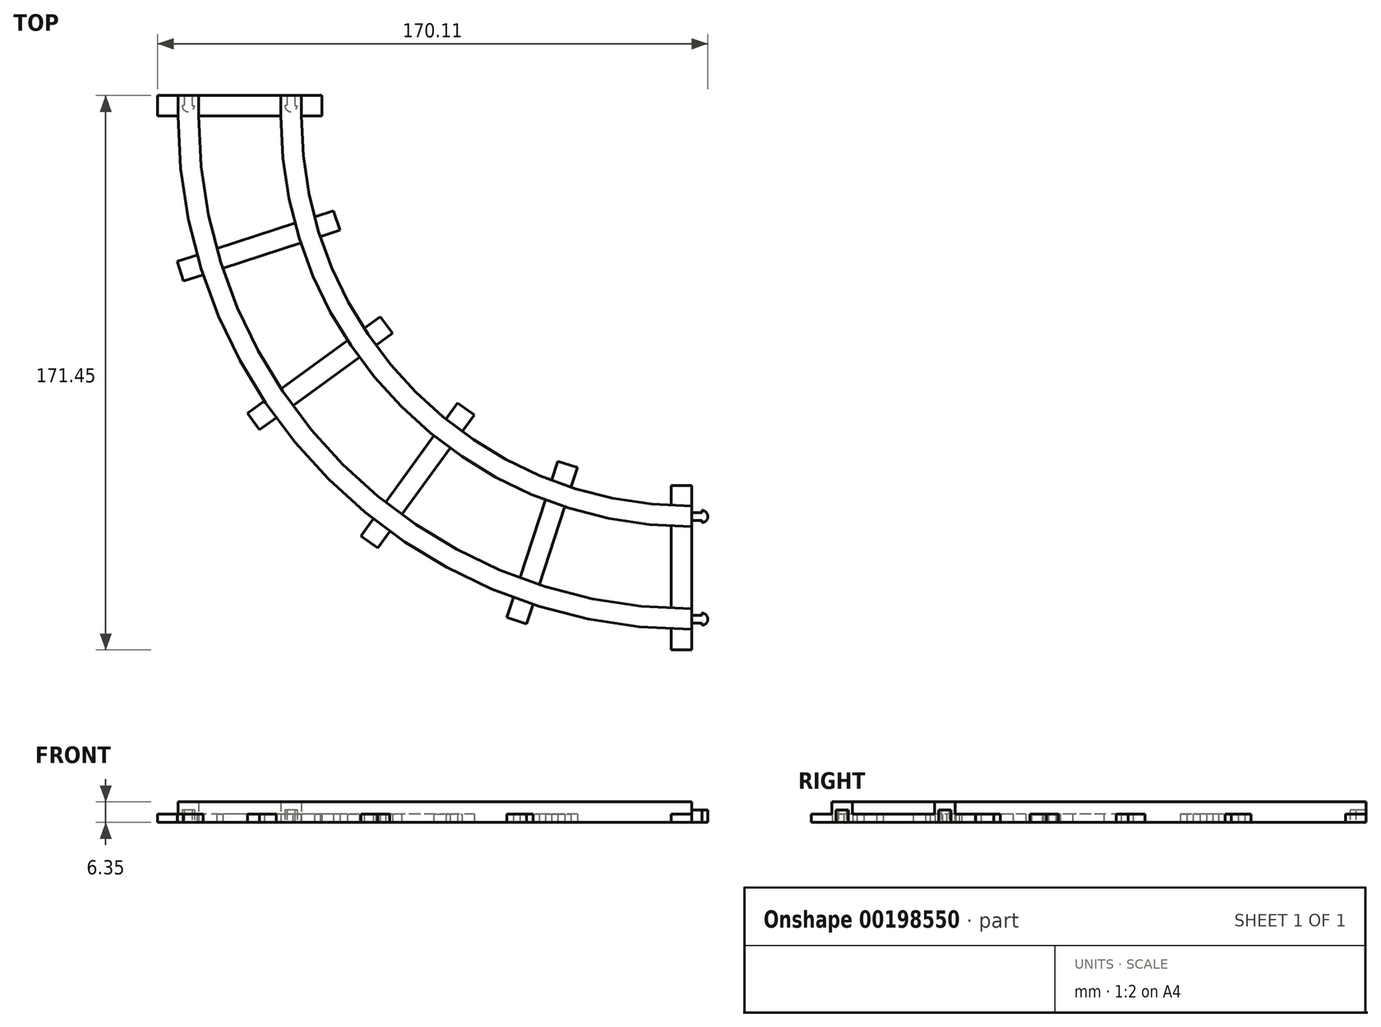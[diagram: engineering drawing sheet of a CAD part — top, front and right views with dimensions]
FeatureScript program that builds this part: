
annotation { "Feature Type Name" : "Feature", "Feature Type Description" : "" }
export const myFeature = defineFeature(function(context is Context, id is Id, definition is map)
    precondition{}
    {
        {
            var Q0;
            Q0=qCreatedBy(makeId("Top.planeOp"),FACE);
            var sketch = newSketch(context, id + "F0", { "sketchPlane" : qUnion([Q0])});
            skLineSegment(sketch, "E0.bottom", {"start": v(76.2, 76.2) * mm, "end": v(-76.2, 76.2) * mm, "construction": true});
            skPoint(sketch, "E0.middle", {"position": v(0, 0) * mm});
            skLineSegment(sketch, "E1", {"start": v(-76.2, 76.2) * mm, "end": v(-76.2, 101.6) * mm, "construction": true});
            skLineSegment(sketch, "E2", {"start": v(76.2, -76.2) * mm, "end": v(101.6, -76.2) * mm, "construction": true});
            skArc(sketch, "E3", {"start": v(76.2, -76.2) * mm, "mid": v(-31.56, -31.56) * mm, "end": v(-76.2, 76.2) * mm});
            skLineSegment(sketch, "E4", {"start": v(-76.2, 76.2) * mm, "end": v(-50.8, 76.2) * mm, "construction": true});
            skLineSegment(sketch, "E5", {"start": v(-50.8, 76.2) * mm, "end": v(-50.8, 101.6) * mm, "construction": true});
            skLineSegment(sketch, "E6", {"start": v(76.2, -76.2) * mm, "end": v(76.2, -50.8) * mm, "construction": true});
            skLineSegment(sketch, "E7", {"start": v(76.2, -50.8) * mm, "end": v(101.6, -50.8) * mm, "construction": true});
            skArc(sketch, "E8", {"start": v(76.2, -50.8) * mm, "mid": v(-13.6, -13.6) * mm, "end": v(-50.8, 76.2) * mm});
            skLineSegment(sketch, "E9", {"start": v(-76.2, 76.2) * mm, "end": v(-82.55, 76.2) * mm, "construction": true});
            skLineSegment(sketch, "E10", {"start": v(76.2, -76.2) * mm, "end": v(76.2, -82.55) * mm, "construction": true});
            skLineSegment(sketch, "E11", {"start": v(76.2, -82.55) * mm, "end": v(101.6, -82.55) * mm, "construction": true});
            skArc(sketch, "E12", {"start": v(76.2, -82.55) * mm, "mid": v(-36.05, -36.05) * mm, "end": v(-82.55, 76.2) * mm});
            skLineSegment(sketch, "E13", {"start": v(-82.55, 76.2) * mm, "end": v(-76.2, 76.2) * mm});
            skLineSegment(sketch, "E14", {"start": v(76.2, -82.55) * mm, "end": v(76.2, -76.2) * mm});
            skLineSegment(sketch, "E15", {"start": v(-50.8, 76.2) * mm, "end": v(-44.45, 76.2) * mm});
            skLineSegment(sketch, "E16", {"start": v(-44.45, 76.2) * mm, "end": v(-44.45, 101.6) * mm, "construction": true});
            skLineSegment(sketch, "E17", {"start": v(76.2, -44.45) * mm, "end": v(101.6, -44.45) * mm, "construction": true});
            skArc(sketch, "E18", {"start": v(76.2, -44.45) * mm, "mid": v(-9.11, -9.11) * mm, "end": v(-44.45, 76.2) * mm});
            skLineSegment(sketch, "E19", {"start": v(76.2, -44.45) * mm, "end": v(76.2, -50.8) * mm});
            skSolve(sketch);
        }
        {
            var Q0;
            Q0 = qSketchRegion(id + "F0", true);
            extrude(context, id + "F1", {"entities" : qUnion([Q0]), "depth" : 6.35 * mm});
        }
        {
            var Q0;
            Q0=qCreatedBy(makeId("Top.planeOp"),FACE);
            var sketch = newSketch(context, id + "F2", { "sketchPlane" : qUnion([Q0])});
            skLineSegment(sketch, "E20.bottom", {"start": v(76.2, 76.2) * mm, "end": v(-76.2, 76.2) * mm, "construction": true});
            skLineSegment(sketch, "E20.top", {"start": v(76.2, -76.2) * mm, "end": v(-76.2, -76.2) * mm, "construction": true});
            skLineSegment(sketch, "E20.right", {"start": v(-76.2, 76.2) * mm, "end": v(-76.2, -76.2) * mm, "construction": true});
            skPoint(sketch, "E20.middle", {"position": v(0, 0) * mm});
            skLineSegment(sketch, "E21", {"start": v(76.2, -76.2) * mm, "end": v(76.2, -88.9) * mm, "construction": true});
            skLineSegment(sketch, "E22", {"start": v(76.2, -76.2) * mm, "end": v(76.2, -38.1) * mm, "construction": true});
            skLineSegment(sketch, "E23", {"start": v(76.2, -38.1) * mm, "end": v(69.85, -38.1) * mm});
            skLineSegment(sketch, "E24", {"start": v(76.2, -88.9) * mm, "end": v(69.85, -88.9) * mm});
            skLineSegment(sketch, "E25", {"start": v(69.85, -38.1) * mm, "end": v(69.85, -88.9) * mm});
            skLineSegment(sketch, "E26", {"start": v(76.2, -38.1) * mm, "end": v(76.2, -88.9) * mm});
            skArc(sketch, "E27.0", {"start": v(76.2, -44.45) * mm, "mid": v(-9.11, -9.11) * mm, "end": v(-44.45, 76.2) * mm, "construction": true});
            skLineSegment(sketch, "E28.1.0", {"start": v(40.88, -32.5) * mm, "end": v(25.18, -80.82) * mm});
            skLineSegment(sketch, "E28.1.1", {"start": v(34.84, -30.54) * mm, "end": v(19.14, -78.86) * mm});
            skLineSegment(sketch, "E28.1.2", {"start": v(40.88, -32.5) * mm, "end": v(34.84, -30.54) * mm});
            skLineSegment(sketch, "E28.1.3", {"start": v(25.18, -80.82) * mm, "end": v(19.14, -78.86) * mm});
            skLineSegment(sketch, "E28.2.0", {"start": v(9.02, -16.27) * mm, "end": v(-20.84, -57.37) * mm});
            skLineSegment(sketch, "E28.2.1", {"start": v(3.88, -12.54) * mm, "end": v(-25.98, -53.64) * mm});
            skLineSegment(sketch, "E28.2.2", {"start": v(9.02, -16.27) * mm, "end": v(3.88, -12.54) * mm});
            skLineSegment(sketch, "E28.2.3", {"start": v(-20.84, -57.37) * mm, "end": v(-25.98, -53.64) * mm});
            skLineSegment(sketch, "E28.3.0", {"start": v(-16.27, 9.02) * mm, "end": v(-57.37, -20.84) * mm});
            skLineSegment(sketch, "E28.3.1", {"start": v(-20, 14.15) * mm, "end": v(-61.1, -15.7) * mm});
            skLineSegment(sketch, "E28.3.2", {"start": v(-16.27, 9.02) * mm, "end": v(-20, 14.15) * mm});
            skLineSegment(sketch, "E28.3.3", {"start": v(-57.37, -20.84) * mm, "end": v(-61.1, -15.7) * mm});
            skLineSegment(sketch, "E28.4.0", {"start": v(-32.5, 40.88) * mm, "end": v(-80.82, 25.18) * mm});
            skLineSegment(sketch, "E28.4.1", {"start": v(-34.47, 46.92) * mm, "end": v(-82.78, 31.22) * mm});
            skLineSegment(sketch, "E28.4.2", {"start": v(-32.5, 40.88) * mm, "end": v(-34.47, 46.92) * mm});
            skLineSegment(sketch, "E28.4.3", {"start": v(-80.82, 25.18) * mm, "end": v(-82.78, 31.22) * mm});
            skLineSegment(sketch, "E28.5.0", {"start": v(-38.1, 76.2) * mm, "end": v(-88.9, 76.2) * mm});
            skLineSegment(sketch, "E28.5.1", {"start": v(-38.1, 82.55) * mm, "end": v(-88.9, 82.55) * mm});
            skLineSegment(sketch, "E28.5.2", {"start": v(-38.1, 76.2) * mm, "end": v(-38.1, 82.55) * mm});
            skLineSegment(sketch, "E28.5.3", {"start": v(-88.9, 76.2) * mm, "end": v(-88.9, 82.55) * mm});
            skLineSegment(sketch, "E28.anchor1", {"start": v(76.2, 76.2) * mm, "end": v(76.2, -88.9) * mm, "construction": true});
            skLineSegment(sketch, "E28.anchor2", {"start": v(76.2, 76.2) * mm, "end": v(-88.9, 76.2) * mm, "construction": true});
            skSolve(sketch);
        }
        {
            var Q0;
            Q0 = qSketchRegion(id + "F2", true);
            extrude(context, id + "F3", {"entities" : qUnion([Q0]), "operationType" : NewBodyOperationType.ADD, "depth" : 2.54 * mm});
        }
        {
            var Q0;
            Q0=qCreatedBy(makeId("Top.planeOp"),FACE);
            var sketch = newSketch(context, id + "F4", { "sketchPlane" : qUnion([Q0])});
            skArc(sketch, "E29.0", {"start": v(76.2, -82.55) * mm, "mid": v(-36.05, -36.05) * mm, "end": v(-82.55, 76.2) * mm, "construction": true});
            skLineSegment(sketch, "E30", {"start": v(-82.55, 76.2) * mm, "end": v(-82.55, 82.55) * mm});
            skArc(sketch, "E31.0", {"start": v(76.2, -44.45) * mm, "mid": v(-9.11, -9.11) * mm, "end": v(-44.45, 76.2) * mm, "construction": true});
            skLineSegment(sketch, "E32", {"start": v(-44.45, 76.2) * mm, "end": v(-44.45, 82.55) * mm});
            skLineSegment(sketch, "E33", {"start": v(-82.55, 82.55) * mm, "end": v(-76.2, 82.55) * mm});
            skLineSegment(sketch, "E34", {"start": v(-44.45, 82.55) * mm, "end": v(-50.8, 82.55) * mm});
            skLineSegment(sketch, "E35", {"start": v(-82.55, 76.2) * mm, "end": v(-76.2, 76.2) * mm});
            skLineSegment(sketch, "E36", {"start": v(-76.2, 76.2) * mm, "end": v(-76.2, 82.55) * mm});
            skLineSegment(sketch, "E37", {"start": v(-44.45, 76.2) * mm, "end": v(-50.8, 76.2) * mm});
            skLineSegment(sketch, "E38", {"start": v(-50.8, 76.2) * mm, "end": v(-50.8, 82.55) * mm});
            skSolve(sketch);
        }
        {
            var Q0;
            Q0 = qSketchRegion(id + "F4", true);
            extrude(context, id + "F5", {"entities" : qUnion([Q0]), "operationType" : NewBodyOperationType.ADD, "depth" : 6.35 * mm});
        }
        {
            var Q0;
            Q0=makeQuery(id+"F3.boolean.opBoolean","MERGE",FACE,{"derivedFrom":[makeQuery(id+"F1.opExtrude","CAP_FACE",FACE,{"disambiguationData":[OSD([sQuery(id+"F0.wireOp",EDGE,"E3"),sQuery(id+"F0.wireOp",EDGE,"E12"),sQuery(id+"F0.wireOp",EDGE,"E13"),sQuery(id+"F0.wireOp",EDGE,"E14")])],"isStart":true}),makeQuery(id+"F1.opExtrude","CAP_FACE",FACE,{"disambiguationData":[OSD([sQuery(id+"F0.wireOp",EDGE,"E8"),sQuery(id+"F0.wireOp",EDGE,"E15"),sQuery(id+"F0.wireOp",EDGE,"E18"),sQuery(id+"F0.wireOp",EDGE,"E19")])],"isStart":true}),makeQuery(id+"F3.opExtrude","CAP_FACE",FACE,{"disambiguationData":[OSD([sQuery(id+"F2.wireOp",EDGE,"E23"),sQuery(id+"F2.wireOp",EDGE,"E24"),sQuery(id+"F2.wireOp",EDGE,"E25"),sQuery(id+"F2.wireOp",EDGE,"E26")])],"isStart":true}),makeQuery(id+"F3.opExtrude","CAP_FACE",FACE,{"disambiguationData":[OSD([sQuery(id+"F2.wireOp",EDGE,"E28.1.0"),sQuery(id+"F2.wireOp",EDGE,"E28.1.1"),sQuery(id+"F2.wireOp",EDGE,"E28.1.2"),sQuery(id+"F2.wireOp",EDGE,"E28.1.3")])],"isStart":true}),makeQuery(id+"F3.opExtrude","CAP_FACE",FACE,{"disambiguationData":[OSD([sQuery(id+"F2.wireOp",EDGE,"E28.2.0"),sQuery(id+"F2.wireOp",EDGE,"E28.2.1"),sQuery(id+"F2.wireOp",EDGE,"E28.2.2"),sQuery(id+"F2.wireOp",EDGE,"E28.2.3")])],"isStart":true}),makeQuery(id+"F3.opExtrude","CAP_FACE",FACE,{"disambiguationData":[OSD([sQuery(id+"F2.wireOp",EDGE,"E28.3.0"),sQuery(id+"F2.wireOp",EDGE,"E28.3.1"),sQuery(id+"F2.wireOp",EDGE,"E28.3.2"),sQuery(id+"F2.wireOp",EDGE,"E28.3.3")])],"isStart":true}),makeQuery(id+"F3.opExtrude","CAP_FACE",FACE,{"disambiguationData":[OSD([sQuery(id+"F2.wireOp",EDGE,"E28.4.0"),sQuery(id+"F2.wireOp",EDGE,"E28.4.1"),sQuery(id+"F2.wireOp",EDGE,"E28.4.2"),sQuery(id+"F2.wireOp",EDGE,"E28.4.3")])],"isStart":true}),makeQuery(id+"F3.opExtrude","CAP_FACE",FACE,{"disambiguationData":[OSD([sQuery(id+"F2.wireOp",EDGE,"E28.5.0"),sQuery(id+"F2.wireOp",EDGE,"E28.5.1"),sQuery(id+"F2.wireOp",EDGE,"E28.5.2"),sQuery(id+"F2.wireOp",EDGE,"E28.5.3")])],"isStart":true})]});
            var sketch = newSketch(context, id + "F6", { "sketchPlane" : qUnion([Q0])});
            skLineSegment(sketch, "E39", {"start": v(76.2, 79.38) * mm, "end": v(79.37, 79.38) * mm, "construction": true});
            skLineSegment(sketch, "E40", {"start": v(76.2, 79.38) * mm, "end": v(76.2, 80.57) * mm});
            skLineSegment(sketch, "E41.MirrorCS", {"start": v(76.2, 79.38) * mm, "end": v(76.2, 78.19) * mm});
            skLineSegment(sketch, "E42", {"start": v(76.2, 80.57) * mm, "end": v(79.38, 80.57) * mm});
            skLineSegment(sketch, "E43", {"start": v(79.38, 80.57) * mm, "end": v(79.38, 81.28) * mm});
            skLineSegment(sketch, "E44.MirrorCS", {"start": v(76.2, 78.19) * mm, "end": v(79.38, 78.19) * mm});
            skLineSegment(sketch, "E45.MirrorCS", {"start": v(79.38, 78.19) * mm, "end": v(79.38, 77.47) * mm});
            skArc(sketch, "E46", {"start": v(79.38, 77.47) * mm, "mid": v(81.21, 79.38) * mm, "end": v(79.38, 81.28) * mm});
            skLineSegment(sketch, "E47", {"start": v(76.2, 88.9) * mm, "end": v(76.2, 80.57) * mm, "construction": true});
            skLineSegment(sketch, "E48", {"start": v(76.2, 88.9) * mm, "end": v(76.2, 38.1) * mm, "construction": true});
            skLineSegment(sketch, "E49", {"start": v(76.2, 63.5) * mm, "end": v(132.1, 63.5) * mm, "construction": true});
            skLineSegment(sketch, "E50.MirrorCS", {"start": v(76.2, 46.43) * mm, "end": v(79.38, 46.43) * mm});
            skLineSegment(sketch, "E51.MirrorCS", {"start": v(76.2, 48.81) * mm, "end": v(79.38, 48.81) * mm});
            skArc(sketch, "E52.MirrorCS", {"start": v(79.38, 49.53) * mm, "mid": v(81.21, 47.62) * mm, "end": v(79.38, 45.72) * mm});
            skLineSegment(sketch, "E53.MirrorCS", {"start": v(79.38, 46.43) * mm, "end": v(79.38, 45.72) * mm});
            skLineSegment(sketch, "E54.MirrorCS", {"start": v(79.38, 48.81) * mm, "end": v(79.38, 49.53) * mm});
            skLineSegment(sketch, "E55.MirrorCS", {"start": v(76.2, 47.62) * mm, "end": v(76.2, 48.81) * mm});
            skLineSegment(sketch, "E56.MirrorCS", {"start": v(76.2, 47.62) * mm, "end": v(76.2, 46.43) * mm});
            skSolve(sketch);
        }
        {
            var Q0;
            Q0 = qSketchRegion(id + "F6", true);
            extrude(context, id + "F7", {"entities" : qUnion([Q0]), "operationType" : NewBodyOperationType.ADD, "oppositeDirection" : true, "depth" : 3.8 * mm});
        }
        {
            var Q0;
            Q0=makeQuery(id+"F7.boolean.opBoolean","MERGE",FACE,{"derivedFrom":[makeQuery(id+"F3.boolean.opBoolean","MERGE",FACE,{"derivedFrom":[makeQuery(id+"F1.opExtrude","CAP_FACE",FACE,{"disambiguationData":[OSD([sQuery(id+"F0.wireOp",EDGE,"E3"),sQuery(id+"F0.wireOp",EDGE,"E12"),sQuery(id+"F0.wireOp",EDGE,"E13"),sQuery(id+"F0.wireOp",EDGE,"E14")])],"isStart":true}),makeQuery(id+"F1.opExtrude","CAP_FACE",FACE,{"disambiguationData":[OSD([sQuery(id+"F0.wireOp",EDGE,"E8"),sQuery(id+"F0.wireOp",EDGE,"E15"),sQuery(id+"F0.wireOp",EDGE,"E18"),sQuery(id+"F0.wireOp",EDGE,"E19")])],"isStart":true}),makeQuery(id+"F3.opExtrude","CAP_FACE",FACE,{"disambiguationData":[OSD([sQuery(id+"F2.wireOp",EDGE,"E23"),sQuery(id+"F2.wireOp",EDGE,"E24"),sQuery(id+"F2.wireOp",EDGE,"E25"),sQuery(id+"F2.wireOp",EDGE,"E26")])],"isStart":true}),makeQuery(id+"F3.opExtrude","CAP_FACE",FACE,{"disambiguationData":[OSD([sQuery(id+"F2.wireOp",EDGE,"E28.1.0"),sQuery(id+"F2.wireOp",EDGE,"E28.1.1"),sQuery(id+"F2.wireOp",EDGE,"E28.1.2"),sQuery(id+"F2.wireOp",EDGE,"E28.1.3")])],"isStart":true}),makeQuery(id+"F3.opExtrude","CAP_FACE",FACE,{"disambiguationData":[OSD([sQuery(id+"F2.wireOp",EDGE,"E28.2.0"),sQuery(id+"F2.wireOp",EDGE,"E28.2.1"),sQuery(id+"F2.wireOp",EDGE,"E28.2.2"),sQuery(id+"F2.wireOp",EDGE,"E28.2.3")])],"isStart":true}),makeQuery(id+"F3.opExtrude","CAP_FACE",FACE,{"disambiguationData":[OSD([sQuery(id+"F2.wireOp",EDGE,"E28.3.0"),sQuery(id+"F2.wireOp",EDGE,"E28.3.1"),sQuery(id+"F2.wireOp",EDGE,"E28.3.2"),sQuery(id+"F2.wireOp",EDGE,"E28.3.3")])],"isStart":true}),makeQuery(id+"F3.opExtrude","CAP_FACE",FACE,{"disambiguationData":[OSD([sQuery(id+"F2.wireOp",EDGE,"E28.4.0"),sQuery(id+"F2.wireOp",EDGE,"E28.4.1"),sQuery(id+"F2.wireOp",EDGE,"E28.4.2"),sQuery(id+"F2.wireOp",EDGE,"E28.4.3")])],"isStart":true}),makeQuery(id+"F3.opExtrude","CAP_FACE",FACE,{"disambiguationData":[OSD([sQuery(id+"F2.wireOp",EDGE,"E28.5.0"),sQuery(id+"F2.wireOp",EDGE,"E28.5.1"),sQuery(id+"F2.wireOp",EDGE,"E28.5.2"),sQuery(id+"F2.wireOp",EDGE,"E28.5.3")])],"isStart":true})]}),makeQuery(id+"F7.opExtrude","CAP_FACE",FACE,{"disambiguationData":[OSD([sQuery(id+"F6.wireOp",EDGE,"E40"),sQuery(id+"F6.wireOp",EDGE,"E41.MirrorCS"),sQuery(id+"F6.wireOp",EDGE,"E42"),sQuery(id+"F6.wireOp",EDGE,"E43"),sQuery(id+"F6.wireOp",EDGE,"E44.MirrorCS"),sQuery(id+"F6.wireOp",EDGE,"E45.MirrorCS"),sQuery(id+"F6.wireOp",EDGE,"E46")])],"isStart":true}),makeQuery(id+"F7.opExtrude","CAP_FACE",FACE,{"disambiguationData":[OSD([sQuery(id+"F6.wireOp",EDGE,"E50.MirrorCS"),sQuery(id+"F6.wireOp",EDGE,"E51.MirrorCS"),sQuery(id+"F6.wireOp",EDGE,"E52.MirrorCS"),sQuery(id+"F6.wireOp",EDGE,"E53.MirrorCS"),sQuery(id+"F6.wireOp",EDGE,"E54.MirrorCS"),sQuery(id+"F6.wireOp",EDGE,"E55.MirrorCS"),sQuery(id+"F6.wireOp",EDGE,"E56.MirrorCS")])],"isStart":true})]});
            var sketch = newSketch(context, id + "F8", { "sketchPlane" : qUnion([Q0])});
            skLineSegment(sketch, "E57", {"start": v(-79.38, -82.55) * mm, "end": v(-79.38, -79.37) * mm, "construction": true});
            skLineSegment(sketch, "E58", {"start": v(-79.38, -82.55) * mm, "end": v(-80.57, -82.55) * mm});
            skLineSegment(sketch, "E59.MirrorCS", {"start": v(-79.38, -82.55) * mm, "end": v(-78.19, -82.55) * mm});
            skLineSegment(sketch, "E60", {"start": v(-80.57, -82.55) * mm, "end": v(-80.57, -79.37) * mm});
            skLineSegment(sketch, "E61", {"start": v(-80.57, -79.37) * mm, "end": v(-81.28, -79.37) * mm});
            skLineSegment(sketch, "E62.MirrorCS", {"start": v(-78.19, -82.55) * mm, "end": v(-78.19, -79.37) * mm});
            skLineSegment(sketch, "E63.MirrorCS", {"start": v(-78.19, -79.37) * mm, "end": v(-77.47, -79.37) * mm});
            skArc(sketch, "E64", {"start": v(-77.47, -79.37) * mm, "mid": v(-79.38, -77.54) * mm, "end": v(-81.28, -79.37) * mm});
            skLineSegment(sketch, "E65", {"start": v(-88.9, -82.55) * mm, "end": v(-80.57, -82.55) * mm, "construction": true});
            skLineSegment(sketch, "E66", {"start": v(-88.9, -82.55) * mm, "end": v(-38.1, -82.55) * mm, "construction": true});
            skLineSegment(sketch, "E67", {"start": v(-63.5, -82.55) * mm, "end": v(-63.5, -51.74) * mm, "construction": true});
            skLineSegment(sketch, "E68.MirrorCS", {"start": v(-48.81, -79.37) * mm, "end": v(-49.53, -79.37) * mm});
            skLineSegment(sketch, "E69.MirrorCS", {"start": v(-46.43, -79.37) * mm, "end": v(-45.72, -79.37) * mm});
            skArc(sketch, "E70.MirrorCS", {"start": v(-49.53, -79.37) * mm, "mid": v(-47.62, -77.54) * mm, "end": v(-45.72, -79.37) * mm});
            skLineSegment(sketch, "E71.MirrorCS", {"start": v(-47.62, -82.55) * mm, "end": v(-47.62, -79.37) * mm, "construction": true});
            skLineSegment(sketch, "E72.MirrorCS", {"start": v(-47.62, -82.55) * mm, "end": v(-46.43, -82.55) * mm});
            skLineSegment(sketch, "E73.MirrorCS", {"start": v(-47.62, -82.55) * mm, "end": v(-48.81, -82.55) * mm});
            skLineSegment(sketch, "E74.MirrorCS", {"start": v(-46.43, -82.55) * mm, "end": v(-46.43, -79.37) * mm});
            skLineSegment(sketch, "E75.MirrorCS", {"start": v(-48.81, -82.55) * mm, "end": v(-48.81, -79.37) * mm});
            skSolve(sketch);
        }
        {
            var Q0;
            Q0 = qSketchRegion(id + "F8", true);
            extrude(context, id + "F9", {"entities" : qUnion([Q0]), "operationType" : NewBodyOperationType.REMOVE, "oppositeDirection" : true, "depth" : 3.8 * mm});
        }
    });
